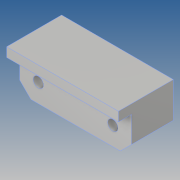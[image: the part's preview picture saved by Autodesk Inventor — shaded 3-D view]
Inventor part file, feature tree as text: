
AUTODESK INVENTOR PART (.ipt)
format: ipt  version: 2018.2 (Build 222227000, 227)  size: 143,360 bytes
history: native  units: mm
features: sketch x5, extrude x2, hole x2, projected_geometry x2, other x1
ambient origin geometry x8: Origin, YZ Plane, XZ Plane, XY Plane, X Axis, Y Axis, Z Axis, Center Point
bodies: Body1 (feature_tree)
feature tree (12):
  other  "200-40-BOGIE-CONNECTOR-03.ipt"
  extrude  "Grundkörper"  Depth=22.5mm TaperAngle=0.0deg
  extrude  "Absatz"  Depth=7.0mm TaperAngle=0.0deg
  hole  "DIN7984_M5_Boh_T2"  [1 undecoded]
  hole  "M5x10"  [1 undecoded]
  sketch  "SkizzeAbsatz"
  sketch  "Skizze5"  dims[d28=10.0mm d29=22.5mm d30=0.0mm]
  sketch  "Skizze7"  dims[d34=5.0mm d35=7.0mm d36=0.0mm]
  projected_geometry  "Projizierte Kontur3"
  sketch  "Skizze10"  dims[d44=4.134mm d45=10.0mm d46=5.0mm d47=2.0mm d48=90.0deg d49=14.2mm d50=20.594885mm]
  projected_geometry  "Projizierte Kontur4"
  sketch  "Skizze11"  dims[d51=5.5mm d52=10.0mm d53=10.0mm d54=2.0mm d55=90.0deg d56=14.2mm d57=20.594885mm]
note: 2 required parameter values undecoded (feature->parameter linkage not recoverable at this tier; creation-order binding heuristic only, values carry confidence <= 0.55)
